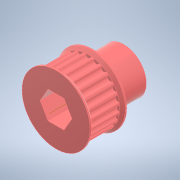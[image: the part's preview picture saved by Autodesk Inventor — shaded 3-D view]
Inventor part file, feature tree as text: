
AUTODESK INVENTOR PART (.ipt)
format: ipt  version: 2022.3 (Build 263350000, 350)  size: 322,560 bytes
history: native  units: in
note: dims shown in document units (in); Inventor stores cm internally (conversion verified against a paired STEP export)
features: extrude x7, sketch x7, mirror x2, chamfer x2, other x1, fillet x1, pattern_circular x1, projected_geometry x1
ambient origin geometry x8: Origin, YZ Plane, XZ Plane, XY Plane, X Axis, Y Axis, Z Axis, Center Point
bodies: Solid1 (feature_tree)
feature tree (22):
  other  "Hex Bore"
  extrude  "HTD Base"  Depth=0.3937in TaperAngle=0.0deg
  extrude  "HTD Flange"  Depth=0.0591in
  mirror  "HTD Flanges"
  chamfer  "HTD Flange Chamfer"  Distance=0.0787in Angle=45.0deg
  extrude  "GT2 Base"  TaperAngle=0.0deg  [1 undecoded]
  extrude  "GT2 Base Tooth"  TaperAngle=0.0deg  [1 undecoded]
  fillet  "GT2 Base Tooth pt. 2"  Radius=0.8723in
  pattern_circular  "GT2 Teeth"  [2 undecoded]
  extrude  "GT2 Flange"  Depth=0.4375in
  mirror  "GT2 Flanges"
  chamfer  "GT2 Flange Chamfer"  Distance=0.0075in
  extrude  "Circle Bore"  TaperAngle=0.0deg  [1 undecoded]
  extrude  "Extrusion9"  Depth=0.0118in
  sketch  "Sketch1"  dims[d0=1.4588in d1=0.3937in d2=0.0in]
  sketch  "Sketch4"  dims[d12=0.0394in d13=0.0591in]
  sketch  "Sketch5"  dims[d14=0.0in]
  sketch  "Sketch6"  dims[d15=0.0394in d16=0.0787in d17=45.0deg]
  sketch  "Sketch7"  dims[d18=0.385in d19=0.0in d20=0.0in]
  sketch  "Sketch8"  dims[d21=0.385in d22=0.0in d23=0.0in d24=0.8723in]
  sketch  "Sketch9"  dims[d25=0.3937in d26=0.0in d27=0.0727in d28=0.0075in d29=0.0in d30=0.0in d31=0.0118in d32=9.4488in d33=360.0deg d35=0.0394in d36=0.0591in d37=0.0in d38=0.0394in d39=0.0787in d40=45.0deg d41=0.625in d42=0.4375in d43=0.0in]
  projected_geometry  "Projected Loop1"
note: 5 required parameter values undecoded (feature->parameter linkage not recoverable at this tier; creation-order binding heuristic only, values carry confidence <= 0.55)
